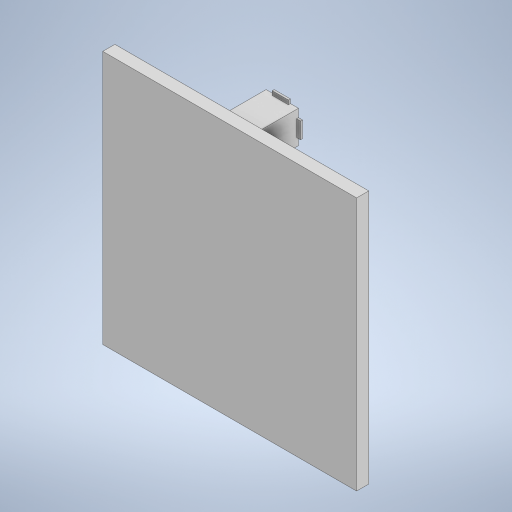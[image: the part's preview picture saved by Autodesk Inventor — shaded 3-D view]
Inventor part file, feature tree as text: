
AUTODESK INVENTOR PART (.ipt)
format: ipt  version: 2024 (Build 280153000, 153)  size: 249,344 bytes
history: native  units: mm
features: extrude x3, sketch x3
ambient origin geometry x8: Origin, YZ Plane, XZ Plane, XY Plane, X Axis, Y Axis, Z Axis, Center Point
bodies: Volumenkörper1 (feature_tree)
feature tree (6):
  extrude  "Extrusion1"  Depth=62.7mm
  extrude  "Extrusion2"  Depth=1.0mm
  extrude  "Extrusion3"  Depth=4.0mm
  sketch  "Skizze1"  dims[d0=62.7mm d1=62.7mm]
  sketch  "Skizze2"  dims[d2=3.0mm d3=0.0mm d6=1.0mm]
  sketch  "Skizze3"  dims[d7=8.0mm d9=4.0mm d10=4.0mm d11=10.0mm d12=0.0mm d16=0.5mm d17=0.0mm d18=1.0mm d19=1.0mm d21=1.0mm d22=1.0mm d23=2.0mm d24=2.0mm d25=2.0mm d26=2.0mm d27=2.0mm d28=2.0mm d29=2.0mm]
